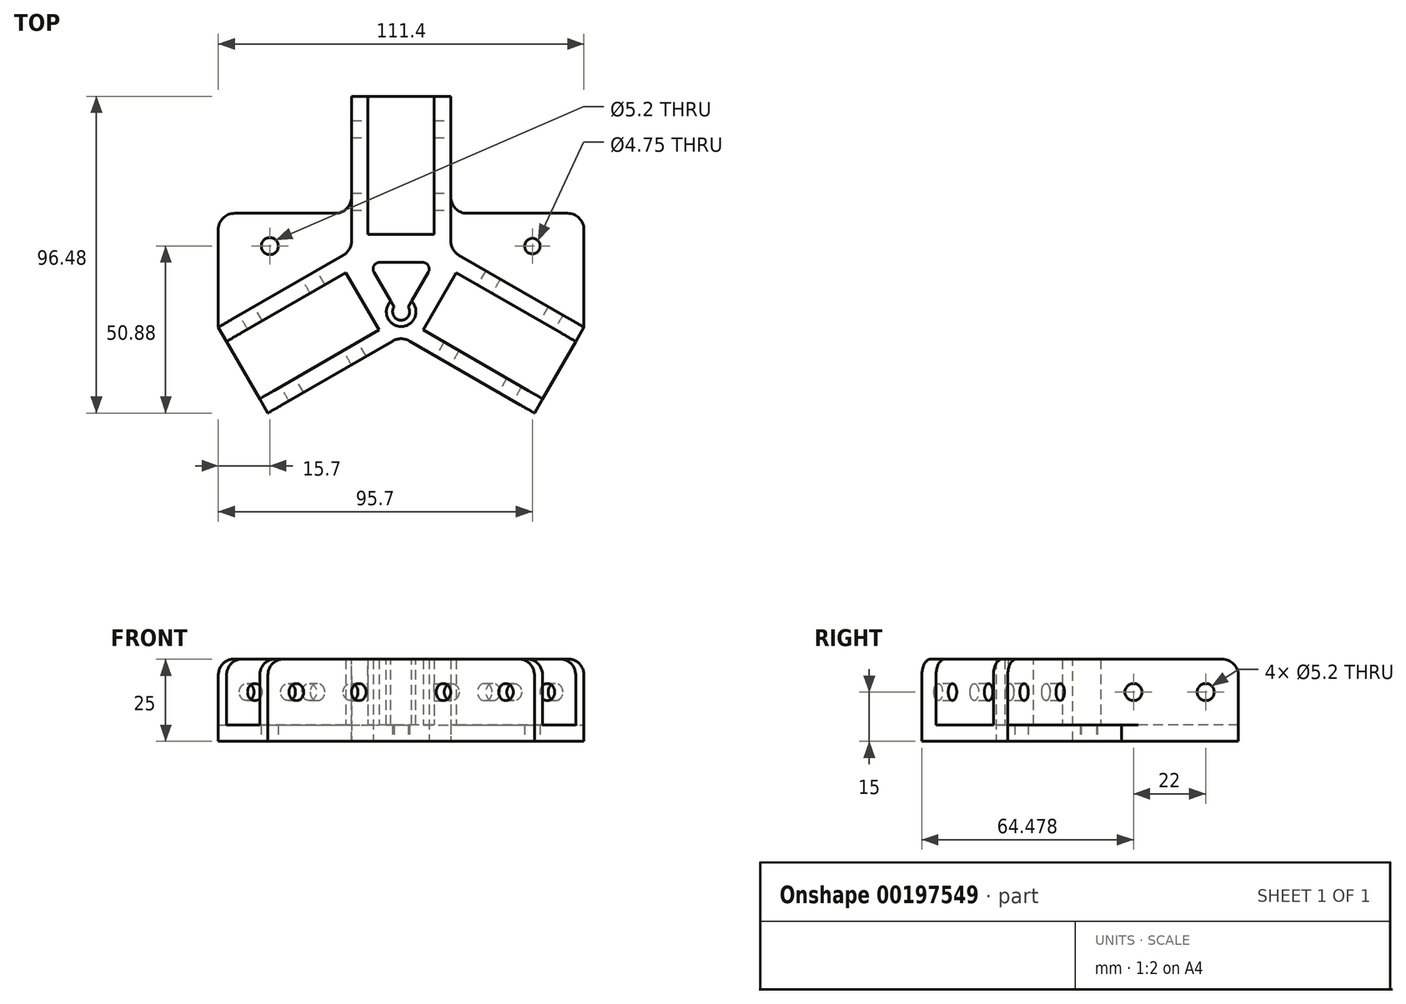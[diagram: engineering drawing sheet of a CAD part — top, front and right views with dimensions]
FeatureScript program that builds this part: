
annotation { "Feature Type Name" : "Feature", "Feature Type Description" : "" }
export const myFeature = defineFeature(function(context is Context, id is Id, definition is map)
    precondition{}
    {
        {
            var Q0;
            Q0=qCreatedBy(makeId("Top.planeOp"),FACE);
            var sketch = newSketch(context, id + "F0", { "sketchPlane" : qUnion([Q0])});
            skLineSegment(sketch, "E0", {"start": v(0, 0) * mm, "end": v(250, -144.34) * mm, "construction": true});
            skLineSegment(sketch, "E1", {"start": v(0, 0) * mm, "end": v(0, 45.49) * mm, "construction": true});
            skLineSegment(sketch, "E2", {"start": v(6.73, -15.55) * mm, "end": v(43.1, -36.55) * mm});
            skLineSegment(sketch, "E3", {"start": v(40.6, -40.88) * mm, "end": v(43.1, -36.55) * mm});
            skLineSegment(sketch, "E4", {"start": v(53.2, -19.05) * mm, "end": v(16.83, 1.95) * mm});
            skLineSegment(sketch, "E5", {"start": v(-0.2, -17.32) * mm, "end": v(40.6, -40.88) * mm});
            skLineSegment(sketch, "E6", {"start": v(55.7, -14.72) * mm, "end": v(14.9, 8.83) * mm});
            skLineSegment(sketch, "E7.trimOffspring", {"start": v(53.2, -19.05) * mm, "end": v(55.7, -14.72) * mm});
            skPoint(sketch, "E8.startSnap0", {"position": v(7.5, -4.33) * mm});
            skPoint(sketch, "E9.orphan", {"position": v(0, -11.66) * mm});
            skLineSegment(sketch, "E10", {"start": v(6.73, -15.55) * mm, "end": v(16.83, 1.95) * mm});
            skLineSegment(sketch, "E11", {"start": v(14.9, 8.83) * mm, "end": v(0, 0) * mm});
            skLineSegment(sketch, "E12", {"start": v(0, 0) * mm, "end": v(-0.2, -17.32) * mm});
            skPoint(sketch, "E13.endSnap0", {"position": v(11.78, -6.8) * mm});
            skLineSegment(sketch, "E14", {"start": v(16.86, 1.81) * mm, "end": v(6.86, -15.5) * mm, "construction": true});
            skLineSegment(sketch, "E15", {"start": v(6.86, -15.5) * mm, "end": v(250, -155.88) * mm, "construction": true});
            skLineSegment(sketch, "E16", {"start": v(250, -132.8) * mm, "end": v(16.86, 1.81) * mm, "construction": true});
            skLineSegment(sketch, "E17.bottom", {"start": v(-152.4, 152.4) * mm, "end": v(152.4, 152.4) * mm, "construction": true});
            skLineSegment(sketch, "E17.top", {"start": v(-152.4, -152.4) * mm, "end": v(152.4, -152.4) * mm, "construction": true});
            skLineSegment(sketch, "E17.left", {"start": v(-152.4, 152.4) * mm, "end": v(-152.4, -152.4) * mm, "construction": true});
            skLineSegment(sketch, "E17.right", {"start": v(152.4, 152.4) * mm, "end": v(152.4, -152.4) * mm, "construction": true});
            skLineSegment(sketch, "E18.bottom", {"start": v(-250, 230) * mm, "end": v(250, 230) * mm, "construction": true});
            skLineSegment(sketch, "E18.top", {"start": v(-250, -230) * mm, "end": v(250, -230) * mm, "construction": true});
            skLineSegment(sketch, "E18.left", {"start": v(-250, 230) * mm, "end": v(-250, -230) * mm, "construction": true});
            skLineSegment(sketch, "E19.top", {"start": v(-250, 250) * mm, "end": v(250, 250) * mm, "construction": true});
            skLineSegment(sketch, "E19.left", {"start": v(-250, 230) * mm, "end": v(-250, 250) * mm, "construction": true});
            skLineSegment(sketch, "E19.right", {"start": v(250, 230) * mm, "end": v(250, 250) * mm, "construction": true});
            skLineSegment(sketch, "E20.bottom", {"start": v(-250, 250) * mm, "end": v(-270, 250) * mm, "construction": true});
            skLineSegment(sketch, "E20.top", {"start": v(-250, -250) * mm, "end": v(-270, -250) * mm, "construction": true});
            skLineSegment(sketch, "E20.left", {"start": v(-250, 250) * mm, "end": v(-250, -250) * mm, "construction": true});
            skLineSegment(sketch, "E20.right", {"start": v(-270, 250) * mm, "end": v(-270, -250) * mm, "construction": true});
            skLineSegment(sketch, "E21.bottom", {"start": v(250, 250) * mm, "end": v(270, 250) * mm, "construction": true});
            skLineSegment(sketch, "E21.top", {"start": v(250, -250) * mm, "end": v(270, -250) * mm, "construction": true});
            skLineSegment(sketch, "E21.left", {"start": v(250, 250) * mm, "end": v(250, -117.97) * mm, "construction": true});
            skLineSegment(sketch, "E21.right", {"start": v(270, 250) * mm, "end": v(270, -250) * mm, "construction": true});
            skLineSegment(sketch, "E22.bottom", {"start": v(-250, -250) * mm, "end": v(250, -250) * mm, "construction": true});
            skLineSegment(sketch, "E22.left", {"start": v(-250, -250) * mm, "end": v(-250, -230) * mm, "construction": true});
            skLineSegment(sketch, "E22.right", {"start": v(250, -250) * mm, "end": v(250, -230) * mm, "construction": true});
            skLineSegment(sketch, "E23", {"start": v(260, -238.46) * mm, "end": v(260, 217.54) * mm, "construction": true});
            skLineSegment(sketch, "E24.trimOffspring", {"start": v(250, -117.97) * mm, "end": v(250, -230) * mm, "construction": true});
            skLineSegment(sketch, "E25.trimOffspring", {"start": v(250, -117.97) * mm, "end": v(250, -250) * mm, "construction": true});
            skLineSegment(sketch, "E26", {"start": v(229.22, -118.48) * mm, "end": v(217.22, -139.27) * mm, "construction": true});
            skLineSegment(sketch, "E27", {"start": v(217.22, -139.27) * mm, "end": v(238, -151.27) * mm, "construction": true});
            skLineSegment(sketch, "E28", {"start": v(238, -151.27) * mm, "end": v(250, -130.48) * mm, "construction": true});
            skLineSegment(sketch, "E29", {"start": v(250, -130.48) * mm, "end": v(229.22, -118.48) * mm, "construction": true});
            skCircle(sketch, "E30", {"center": v(233.6, -134.87) * mm, "radius": 9.55 * mm, "construction": true});
            skCircle(sketch, "E31", {"center": v(233.6, -134.87) * mm, "radius": 6 * mm, "construction": true});
            skPoint(sketch, "E32", {"position": v(152.4, -87.99) * mm});
            skSolve(sketch);
        }
        {
            var Q0;
            Q0=qSketchRegion(id+"F0",true);
            extrude(context, id + "F1", {"entities" : qUnion([Q0]), "depth" : 20 * mm});
        }
        {
            var Q0;
            Q0=makeQuery(id+"F8AnNkQhTy7cih4_3.boolean.opBoolean","MERGE",FACE,{"derivedFrom":[makeQuery(id+"F1.opExtrude","SWEPT_FACE",FACE,{"disambiguationData":[OSD([sQuery(id+"F0.wireOp",EDGE,"E5")])]}),makeQuery(id+"F8AnNkQhTy7cih4_3.opExtrude","SWEPT_FACE",FACE,{"disambiguationData":[OSD([sQuery(id+"FXKs39bWKYu9lIt_3.wireOp",EDGE,"d46a372c-ea87-446f-ae03-e79ca4958cda.0")])]})]});
            var sketch = newSketch(context, id + "F2", { "sketchPlane" : qUnion([Q0])});
            skCircle(sketch, "E33", {"center": v(45.6, 10) * mm, "radius": 2.6 * mm});
            skCircle(sketch, "E34", {"center": v(23.6, 10) * mm, "radius": 2.6 * mm});
            skSolve(sketch);
        }
        {
            var Q0;
            Q0=qSketchRegion(id+"F2",true);
            extrude(context, id + "F3", {"entities" : qUnion([Q0]), "operationType" : NewBodyOperationType.REMOVE, "endBound" : BoundingType.THROUGH_ALL, "oppositeDirection" : true, "depth" : 25 * mm});
        }
        {
            var Q0;
            Q0=makeQuery(id+"F1.opExtrude","SWEPT_BODY",BODY,{"disambiguationData":[OSD([sQuery(id+"F0.wireOp",EDGE,"E2"),sQuery(id+"F0.wireOp",EDGE,"E3"),sQuery(id+"F0.wireOp",EDGE,"E4"),sQuery(id+"F0.wireOp",EDGE,"E5"),sQuery(id+"F0.wireOp",EDGE,"E6"),sQuery(id+"F0.wireOp",EDGE,"E7.trimOffspring"),sQuery(id+"F0.wireOp",EDGE,"E10"),sQuery(id+"F0.wireOp",EDGE,"E11"),sQuery(id+"F0.wireOp",EDGE,"E12")])]});
            var Q1;
            Q1=makeQuery(id+"F1.opExtrude","SWEPT_EDGE",EDGE,{"disambiguationData":[OSD([sQuery(id+"F0.wireOp",EDGE,"E11"),sQuery(id+"F0.wireOp",EDGE,"E12")])]});
            circularPattern(context, id + "F4", {"operationType" : NewBodyOperationType.ADD, "entities" : qUnion([Q0]), "axis" : qUnion([Q1]), "angle" : 120 * degree, "instanceCount" : round(3)});
        }
        {
            var Q0;
            {var subQ0=makeQuery(id+"F1.opExtrude","CAP_FACE",FACE,{"disambiguationData":[OSD([sQuery(id+"F0.wireOp",EDGE,"E2"),sQuery(id+"F0.wireOp",EDGE,"E3"),sQuery(id+"F0.wireOp",EDGE,"E4"),sQuery(id+"F0.wireOp",EDGE,"E5"),sQuery(id+"F0.wireOp",EDGE,"E6"),sQuery(id+"F0.wireOp",EDGE,"E7.trimOffspring"),sQuery(id+"F0.wireOp",EDGE,"E10"),sQuery(id+"F0.wireOp",EDGE,"E11"),sQuery(id+"F0.wireOp",EDGE,"E12")])],"isStart":true});Q0=makeQuery(id+"F4.boolean.opBoolean","MERGE",FACE,{"derivedFrom":[subQ0,makeQuery(id+"F4.opPattern","COPY",FACE,{"derivedFrom":subQ0,"instanceName":"1"}),makeQuery(id+"F4.opPattern","COPY",FACE,{"derivedFrom":subQ0,"instanceName":"2"})]});}
            var sketch = newSketch(context, id + "F5", { "sketchPlane" : qUnion([Q0])});
            skLineSegment(sketch, "E35.0", {"start": v(-40.6, 40.88) * mm, "end": v(0, 17.44) * mm});
            skLineSegment(sketch, "E36.0", {"start": v(0, 17.44) * mm, "end": v(40.6, 40.88) * mm});
            skLineSegment(sketch, "E37.0", {"start": v(55.7, 14.72) * mm, "end": v(15.1, -8.72) * mm});
            skLineSegment(sketch, "E38.0", {"start": v(15.1, -8.72) * mm, "end": v(15.1, -55.6) * mm});
            skLineSegment(sketch, "E39.0", {"start": v(-15.1, -55.6) * mm, "end": v(-15.1, -8.72) * mm});
            skLineSegment(sketch, "E40.0", {"start": v(-15.1, -8.72) * mm, "end": v(-55.7, 14.72) * mm});
            skLineSegment(sketch, "E41", {"start": v(-40.6, 40.88) * mm, "end": v(-55.7, 14.72) * mm});
            skLineSegment(sketch, "E42", {"start": v(40.6, 40.88) * mm, "end": v(55.7, 14.72) * mm});
            skLineSegment(sketch, "E43", {"start": v(15.1, -55.6) * mm, "end": v(-15.1, -55.6) * mm});
            skSolve(sketch);
        }
        {
            var Q0;
            Q0=qSketchRegion(id+"F5",true);
            extrude(context, id + "F6", {"entities" : qUnion([Q0]), "operationType" : NewBodyOperationType.ADD, "depth" : 5 * mm});
        }
        {
            var Q0;
            Q0=makeQuery(id+"F6.boolean.opBoolean","MERGE",EDGE,{"derivedFrom":[makeQuery(id+"F4.boolean.opBoolean","INTERSECT",EDGE,{"derivedFrom":[makeQuery(id+"F1.opExtrude","SWEPT_FACE",FACE,{"disambiguationData":[OSD([sQuery(id+"F0.wireOp",EDGE,"E5")])]}),makeQuery(id+"F4.opPattern","COPY",FACE,{"derivedFrom":makeQuery(id+"F1.opExtrude","SWEPT_FACE",FACE,{"disambiguationData":[OSD([sQuery(id+"F0.wireOp",EDGE,"E6")])]}),"instanceName":"1"})]}),makeQuery(id+"F6.opExtrude","SWEPT_EDGE",EDGE,{"disambiguationData":[OSD([sQuery(id+"F5.wireOp",EDGE,"E35.0"),sQuery(id+"F5.wireOp",EDGE,"E36.0")])]})]});
            var Q1;
            Q1=makeQuery(id+"F6.boolean.opBoolean","MERGE",EDGE,{"derivedFrom":[makeQuery(id+"F4.boolean.opBoolean","INTERSECT",EDGE,{"derivedFrom":[makeQuery(id+"F1.opExtrude","SWEPT_FACE",FACE,{"disambiguationData":[OSD([sQuery(id+"F0.wireOp",EDGE,"E6")])]}),makeQuery(id+"F4.opPattern","COPY",FACE,{"derivedFrom":makeQuery(id+"F1.opExtrude","SWEPT_FACE",FACE,{"disambiguationData":[OSD([sQuery(id+"F0.wireOp",EDGE,"E5")])]}),"instanceName":"2"})]}),makeQuery(id+"F6.opExtrude","SWEPT_EDGE",EDGE,{"disambiguationData":[OSD([sQuery(id+"F5.wireOp",EDGE,"E37.0"),sQuery(id+"F5.wireOp",EDGE,"E38.0")])]})]});
            var Q2;
            Q2=makeQuery(id+"F6.boolean.opBoolean","MERGE",EDGE,{"derivedFrom":[makeQuery(id+"F4.boolean.opBoolean","INTERSECT",EDGE,{"derivedFrom":[makeQuery(id+"F4.opPattern","COPY",FACE,{"derivedFrom":makeQuery(id+"F1.opExtrude","SWEPT_FACE",FACE,{"disambiguationData":[OSD([sQuery(id+"F0.wireOp",EDGE,"E5")])]}),"instanceName":"1"}),makeQuery(id+"F4.opPattern","COPY",FACE,{"derivedFrom":makeQuery(id+"F1.opExtrude","SWEPT_FACE",FACE,{"disambiguationData":[OSD([sQuery(id+"F0.wireOp",EDGE,"E6")])]}),"instanceName":"2"})]}),makeQuery(id+"F6.opExtrude","SWEPT_EDGE",EDGE,{"disambiguationData":[OSD([sQuery(id+"F5.wireOp",EDGE,"E39.0"),sQuery(id+"F5.wireOp",EDGE,"E40.0")])]})]});
            fillet(context, id + "F7", {"entities" : qUnion([Q0, Q1, Q2]), "radius" : 5 * mm, "tangentPropagation" : true, "allowEdgeOverflow" : false});
        }
        {
            var Q0;
            {var subQ0=makeQuery(id+"F1.opExtrude","CAP_FACE",FACE,{"disambiguationData":[OSD([sQuery(id+"F0.wireOp",EDGE,"E2"),sQuery(id+"F0.wireOp",EDGE,"E3"),sQuery(id+"F0.wireOp",EDGE,"E4"),sQuery(id+"F0.wireOp",EDGE,"E5"),sQuery(id+"F0.wireOp",EDGE,"E6"),sQuery(id+"F0.wireOp",EDGE,"E7.trimOffspring"),sQuery(id+"F0.wireOp",EDGE,"E10"),sQuery(id+"F0.wireOp",EDGE,"E11"),sQuery(id+"F0.wireOp",EDGE,"E12")])],"isStart":false});Q0=makeQuery(id+"F4.boolean.opBoolean","MERGE",FACE,{"derivedFrom":[subQ0,makeQuery(id+"F4.opPattern","COPY",FACE,{"derivedFrom":subQ0,"instanceName":"1"}),makeQuery(id+"F4.opPattern","COPY",FACE,{"derivedFrom":subQ0,"instanceName":"2"})]});}
            var sketch = newSketch(context, id + "F8", { "sketchPlane" : qUnion([Q0])});
            skLineSegment(sketch, "E44", {"start": v(-10, 5.06) * mm, "end": v(0, -12.26) * mm});
            skLineSegment(sketch, "E45", {"start": v(0, -12.26) * mm, "end": v(10, 5.06) * mm});
            skLineSegment(sketch, "E46", {"start": v(10, 5.06) * mm, "end": v(-10, 5.06) * mm});
            skSolve(sketch);
        }
        {
            var Q0;
            Q0=makeQuery(id+"F6.opExtrude","CAP_FACE",FACE,{"disambiguationData":[OSD([sQuery(id+"F5.wireOp",EDGE,"E35.0"),sQuery(id+"F5.wireOp",EDGE,"E36.0"),sQuery(id+"F5.wireOp",EDGE,"E37.0"),sQuery(id+"F5.wireOp",EDGE,"E38.0"),sQuery(id+"F5.wireOp",EDGE,"E39.0"),sQuery(id+"F5.wireOp",EDGE,"E40.0"),sQuery(id+"F5.wireOp",EDGE,"E41"),sQuery(id+"F5.wireOp",EDGE,"E42"),sQuery(id+"F5.wireOp",EDGE,"E43")])],"isStart":false});
            var sketch = newSketch(context, id + "F9", { "sketchPlane" : qUnion([Q0])});
            skLineSegment(sketch, "E47.top", {"start": v(-55.7, -20) * mm, "end": v(55.7, -20) * mm});
            skLineSegment(sketch, "E47.left", {"start": v(-55.7, 14.72) * mm, "end": v(-55.7, -20) * mm});
            skLineSegment(sketch, "E47.right", {"start": v(55.7, 14.72) * mm, "end": v(55.7, -20) * mm});
            skLineSegment(sketch, "E48", {"start": v(-52.65, 20) * mm, "end": v(-4.44, 20) * mm});
            skLineSegment(sketch, "E49", {"start": v(52.65, 20) * mm, "end": v(55.7, 14.72) * mm});
            skPoint(sketch, "E50.start.orphan", {"position": v(-52.65, 20) * mm});
            skLineSegment(sketch, "E51", {"start": v(-52.65, 20) * mm, "end": v(-55.7, 14.72) * mm});
            skPoint(sketch, "E52.orphan", {"position": v(-55.7, 20) * mm});
            skArc(sketch, "E53.0", {"start": v(2.5, 18.88) * mm, "mid": v(0, 18.2) * mm, "end": v(-2.5, 18.88) * mm});
            skLineSegment(sketch, "E53.1", {"start": v(2.5, 18.88) * mm, "end": v(4.44, 20) * mm});
            skLineSegment(sketch, "E53.2", {"start": v(-4.44, 20) * mm, "end": v(-2.5, 18.88) * mm});
            skPoint(sketch, "E54.orphan", {"position": v(-40.6, 40.88) * mm});
            skPoint(sketch, "E55.orphan", {"position": v(40.6, 40.88) * mm});
            skLineSegment(sketch, "E56.trimOffspring", {"start": v(4.44, 20) * mm, "end": v(52.65, 20) * mm});
            skSolve(sketch);
        }
        {
            var Q0;
            Q0=qSketchRegion(id+"F9",true);
            extrude(context, id + "F10", {"entities" : qUnion([Q0]), "operationType" : NewBodyOperationType.ADD, "oppositeDirection" : true, "depth" : 5 * mm});
        }
        {
            var Q0;
            Q0=qSketchRegion(id+"F8",true);
            extrude(context, id + "F11", {"entities" : qUnion([Q0]), "operationType" : NewBodyOperationType.REMOVE, "endBound" : BoundingType.THROUGH_ALL, "oppositeDirection" : true, "depth" : 25 * mm});
        }
        {
            var Q0;
            Q0=makeQuery(id+"F11.boolean.opBoolean","COPY",EDGE,{"derivedFrom":makeQuery(id+"F11.opExtrude","SWEPT_EDGE",EDGE,{"disambiguationData":[OSD([sQuery(id+"F8.wireOp",EDGE,"E45"),sQuery(id+"F8.wireOp",EDGE,"E46")])]})});
            var Q1;
            Q1=makeQuery(id+"F11.boolean.opBoolean","COPY",EDGE,{"derivedFrom":makeQuery(id+"F11.opExtrude","SWEPT_EDGE",EDGE,{"disambiguationData":[OSD([sQuery(id+"F8.wireOp",EDGE,"E44"),sQuery(id+"F8.wireOp",EDGE,"E46")])]})});
            var Q2;
            Q2=makeQuery(id+"F11.boolean.opBoolean","COPY",EDGE,{"derivedFrom":makeQuery(id+"F11.opExtrude","SWEPT_EDGE",EDGE,{"disambiguationData":[OSD([sQuery(id+"F8.wireOp",EDGE,"E44"),sQuery(id+"F8.wireOp",EDGE,"E45")])]})});
            fillet(context, id + "F12", {"entities" : qUnion([Q0, Q1, Q2]), "radius" : 2 * mm, "tangentPropagation" : true, "allowEdgeOverflow" : false});
        }
        {
            var Q0;
            Q0=makeQuery(id+"F10.boolean.opBoolean","MERGE",FACE,{"derivedFrom":[makeQuery(id+"F6.opExtrude","CAP_FACE",FACE,{"disambiguationData":[OSD([sQuery(id+"F5.wireOp",EDGE,"E35.0"),sQuery(id+"F5.wireOp",EDGE,"E36.0"),sQuery(id+"F5.wireOp",EDGE,"E37.0"),sQuery(id+"F5.wireOp",EDGE,"E38.0"),sQuery(id+"F5.wireOp",EDGE,"E39.0"),sQuery(id+"F5.wireOp",EDGE,"E40.0"),sQuery(id+"F5.wireOp",EDGE,"E41"),sQuery(id+"F5.wireOp",EDGE,"E42"),sQuery(id+"F5.wireOp",EDGE,"E43")])],"isStart":false}),makeQuery(id+"F10.opExtrude","CAP_FACE",FACE,{"disambiguationData":[OSD([sQuery(id+"F9.wireOp",EDGE,"E47.bottom"),sQuery(id+"F9.wireOp",EDGE,"E47.top"),sQuery(id+"F9.wireOp",EDGE,"E47.left"),sQuery(id+"F9.wireOp",EDGE,"E47.right")])],"isStart":true})]});
            var sketch = newSketch(context, id + "F13", { "sketchPlane" : qUnion([Q0])});
            skCircle(sketch, "E57", {"center": v(-40, -10) * mm, "radius": 2.6 * mm});
            skCircle(sketch, "E58", {"center": v(40, -10) * mm, "radius": 2.37 * mm});
            skCircle(sketch, "E59", {"center": v(0, 10) * mm, "radius": 2.6 * mm});
            skSolve(sketch);
        }
        {
            var Q0;
            Q0=qSketchRegion(id+"F13",true);
            extrude(context, id + "F14", {"entities" : qUnion([Q0]), "operationType" : NewBodyOperationType.REMOVE, "endBound" : BoundingType.THROUGH_ALL, "oppositeDirection" : true, "depth" : 25 * mm});
        }
        {
            var Q0;
            Q0=makeQuery(id+"F10.boolean.opBoolean","INTERSECT",EDGE,{"derivedFrom":[makeQuery(id+"F6.boolean.opBoolean","MERGE",FACE,{"derivedFrom":[makeQuery(id+"F4.opPattern","COPY",FACE,{"derivedFrom":makeQuery(id+"F1.opExtrude","SWEPT_FACE",FACE,{"disambiguationData":[OSD([sQuery(id+"F0.wireOp",EDGE,"E6")])]}),"instanceName":"2"}),makeQuery(id+"F6.opExtrude","SWEPT_FACE",FACE,{"disambiguationData":[OSD([sQuery(id+"F5.wireOp",EDGE,"E39.0")])]})]}),makeQuery(id+"F10.opExtrude","SWEPT_FACE",FACE,{"disambiguationData":[OSD([sQuery(id+"F9.wireOp",EDGE,"E47.top")])]})]});
            var Q1;
            Q1=makeQuery(id+"F10.boolean.opBoolean","INTERSECT",EDGE,{"derivedFrom":[makeQuery(id+"F6.boolean.opBoolean","MERGE",FACE,{"derivedFrom":[makeQuery(id+"F4.opPattern","COPY",FACE,{"derivedFrom":makeQuery(id+"F1.opExtrude","SWEPT_FACE",FACE,{"disambiguationData":[OSD([sQuery(id+"F0.wireOp",EDGE,"E5")])]}),"instanceName":"2"}),makeQuery(id+"F6.opExtrude","SWEPT_FACE",FACE,{"disambiguationData":[OSD([sQuery(id+"F5.wireOp",EDGE,"E38.0")])]})]}),makeQuery(id+"F10.opExtrude","SWEPT_FACE",FACE,{"disambiguationData":[OSD([sQuery(id+"F9.wireOp",EDGE,"E47.top")])]})]});
            var Q2;
            Q2=makeQuery(id+"F10.opExtrude","SWEPT_EDGE",EDGE,{"disambiguationData":[OSD([sQuery(id+"F9.wireOp",EDGE,"E47.top"),sQuery(id+"F9.wireOp",EDGE,"E47.right")])]});
            var Q3;
            Q3=makeQuery(id+"F10.opExtrude","SWEPT_EDGE",EDGE,{"disambiguationData":[OSD([sQuery(id+"F9.wireOp",EDGE,"E47.top"),sQuery(id+"F9.wireOp",EDGE,"E47.left")])]});
            var Q4;
            Q4=makeQuery(id+"F4.opPattern","COPY",EDGE,{"derivedFrom":makeQuery(id+"F1.opExtrude","CAP_EDGE",EDGE,{"disambiguationData":[OSD([sQuery(id+"F0.wireOp",EDGE,"E7.trimOffspring")])],"isStart":false}),"instanceName":"2"});
            var Q5;
            Q5=makeQuery(id+"F4.opPattern","COPY",EDGE,{"derivedFrom":makeQuery(id+"F1.opExtrude","CAP_EDGE",EDGE,{"disambiguationData":[OSD([sQuery(id+"F0.wireOp",EDGE,"E3")])],"isStart":false}),"instanceName":"2"});
            var Q6;
            Q6=makeQuery(id+"F4.opPattern","COPY",EDGE,{"derivedFrom":makeQuery(id+"F1.opExtrude","CAP_EDGE",EDGE,{"disambiguationData":[OSD([sQuery(id+"F0.wireOp",EDGE,"E3")])],"isStart":false}),"instanceName":"1"});
            var Q7;
            Q7=makeQuery(id+"F4.opPattern","COPY",EDGE,{"derivedFrom":makeQuery(id+"F1.opExtrude","CAP_EDGE",EDGE,{"disambiguationData":[OSD([sQuery(id+"F0.wireOp",EDGE,"E7.trimOffspring")])],"isStart":false}),"instanceName":"1"});
            var Q8;
            Q8=makeQuery(id+"F1.opExtrude","CAP_EDGE",EDGE,{"disambiguationData":[OSD([sQuery(id+"F0.wireOp",EDGE,"E7.trimOffspring")])],"isStart":false});
            var Q9;
            Q9=makeQuery(id+"F1.opExtrude","CAP_EDGE",EDGE,{"disambiguationData":[OSD([sQuery(id+"F0.wireOp",EDGE,"E3")])],"isStart":false});
            var Q10;
            Q10=makeQuery(id+"F10.opExtrude","SWEPT_EDGE",EDGE,{"disambiguationData":[OSD([sQuery(id+"F9.wireOp",EDGE,"E47.left"),sQuery(id+"F9.wireOp",EDGE,"E48")])]});
            var Q11;
            Q11=makeQuery(id+"F10.opExtrude","SWEPT_EDGE",EDGE,{"disambiguationData":[OSD([sQuery(id+"F9.wireOp",EDGE,"E47.right"),sQuery(id+"F9.wireOp",EDGE,"E48")])]});
            fillet(context, id + "F15", {"entities" : qUnion([Q0, Q1, Q2, Q3, Q4, Q5, Q6, Q7, Q8, Q9, Q10, Q11]), "radius" : 5 * mm, "tangentPropagation" : true, "allowEdgeOverflow" : false});
        }
        {
            var Q0;
            {var subQ0=makeQuery(id+"F1.opExtrude","CAP_FACE",FACE,{"disambiguationData":[OSD([sQuery(id+"F0.wireOp",EDGE,"E2"),sQuery(id+"F0.wireOp",EDGE,"E3"),sQuery(id+"F0.wireOp",EDGE,"E4"),sQuery(id+"F0.wireOp",EDGE,"E5"),sQuery(id+"F0.wireOp",EDGE,"E6"),sQuery(id+"F0.wireOp",EDGE,"E7.trimOffspring"),sQuery(id+"F0.wireOp",EDGE,"E10"),sQuery(id+"F0.wireOp",EDGE,"E11"),sQuery(id+"F0.wireOp",EDGE,"E12")])],"isStart":false});Q0=makeQuery(id+"F4.boolean.opBoolean","MERGE",FACE,{"derivedFrom":[subQ0,makeQuery(id+"F4.opPattern","COPY",FACE,{"derivedFrom":subQ0,"instanceName":"1"}),makeQuery(id+"F4.opPattern","COPY",FACE,{"derivedFrom":subQ0,"instanceName":"2"})]});}
            var sketch = newSketch(context, id + "F16", { "sketchPlane" : qUnion([Q0])});
            skLineSegment(sketch, "E60.0", {"start": v(-2.15, -8.54) * mm, "end": v(-2.15, -8.54) * mm});
            skCircle(sketch, "E61", {"center": v(0, -10) * mm, "radius": 4.5 * mm});
            skSolve(sketch);
        }
        {
            var Q0;
            Q0=qSketchRegion(id+"F16",true);
            extrude(context, id + "F17", {"entities" : qUnion([Q0]), "operationType" : NewBodyOperationType.REMOVE, "oppositeDirection" : true, "depth" : 20 * mm});
        }
    });
